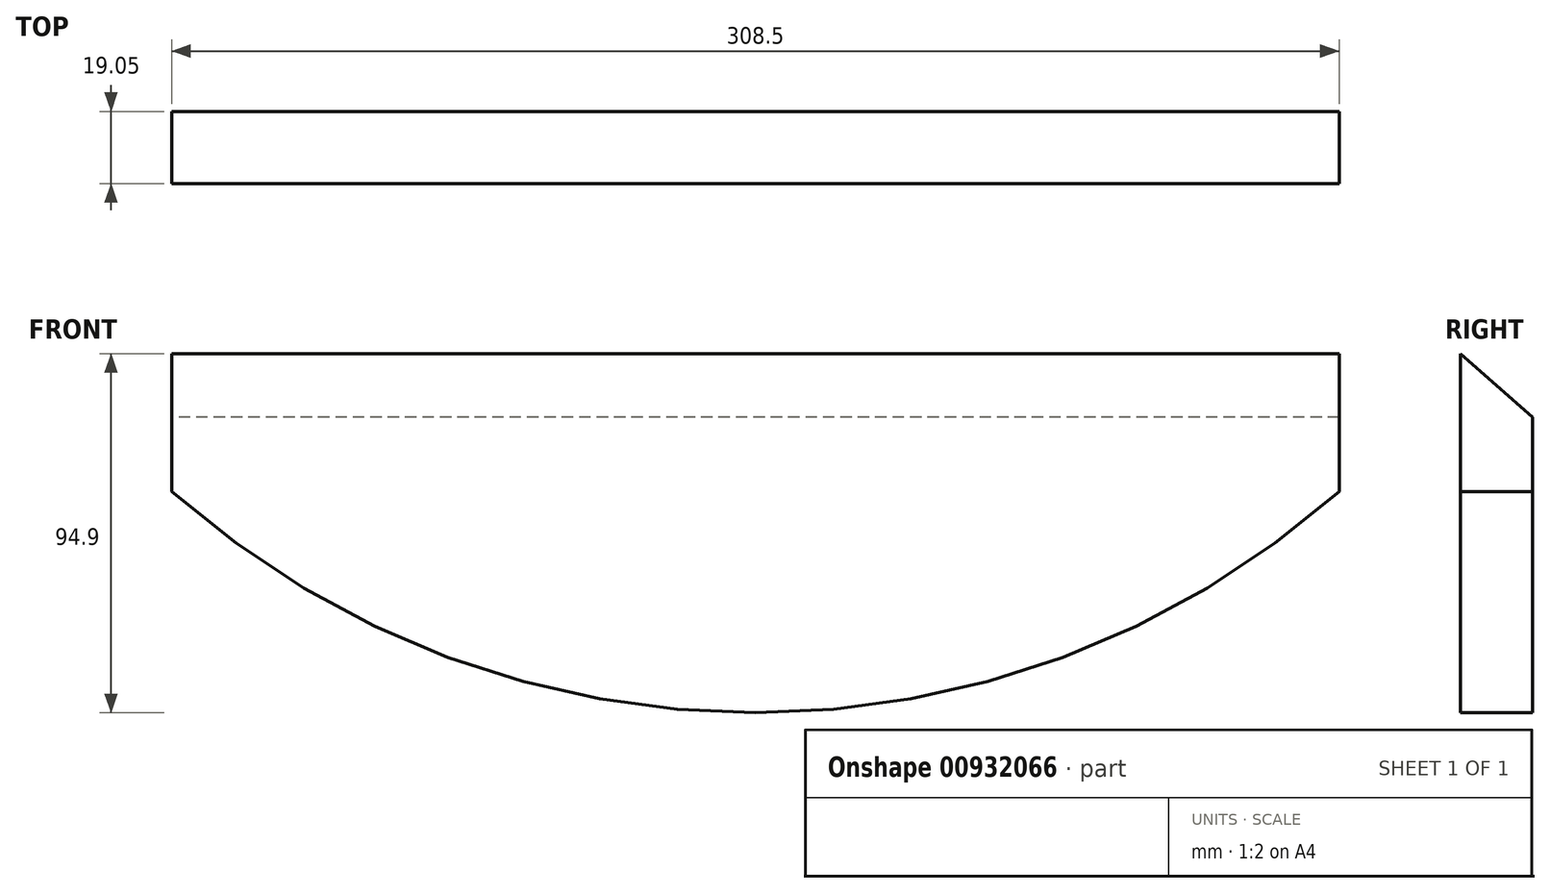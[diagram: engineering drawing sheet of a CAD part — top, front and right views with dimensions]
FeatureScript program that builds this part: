
annotation { "Feature Type Name" : "Feature", "Feature Type Description" : "" }
export const myFeature = defineFeature(function(context is Context, id is Id, definition is map)
    precondition{}
    {
        {
            var Q0;
            Q0=qCreatedBy(makeId("Front.planeOp"),FACE);
            var sketch = newSketch(context, id + "F0", { "sketchPlane" : qUnion([Q0])});
            skLineSegment(sketch, "E0", {"start": v(-154.25, 0) * mm, "end": v(154.25, 0) * mm});
            skArc(sketch, "E1", {"start": v(-154.25, -36.38) * mm, "mid": v(0, -94.9) * mm, "end": v(154.25, -36.38) * mm});
            skPoint(sketch, "E2", {"position": v(0, -94.9) * mm});
            skLineSegment(sketch, "E3", {"start": v(0, 137.66) * mm, "end": v(-110.88, -66.77) * mm, "construction": true});
            skLineSegment(sketch, "E4", {"start": v(-154.25, 0) * mm, "end": v(-154.25, -36.38) * mm});
            skLineSegment(sketch, "E5", {"start": v(154.25, 0) * mm, "end": v(154.25, -36.38) * mm});
            skLineSegment(sketch, "E6", {"start": v(-154.25, -18.2) * mm, "end": v(0, -18.2) * mm, "construction": true});
            skPoint(sketch, "E6.endSnap0", {"position": v(154.25, -18.2) * mm});
            skLineSegment(sketch, "E7", {"start": v(0, -18.2) * mm, "end": v(154.25, -18.2) * mm, "construction": true});
            skPoint(sketch, "E8.orphan", {"position": v(-187.44, 0) * mm});
            skSolve(sketch);
        }
        {
            var Q0;
            Q0 = qSketchRegion(id + "F0", true);
            extrude(context, id + "F1", {"entities" : qUnion([Q0]), "depth" : 19.05 * mm, "offsetDistance" : 25.4 * mm});
        }
        {
            var Q0;
            Q0=makeQuery(id+"F1.opExtrude","SWEPT_FACE",FACE,{"disambiguationData":[OSD([sQuery(id+"F0.wireOp",EDGE,"E4")])]});
            var sketch = newSketch(context, id + "F2", { "sketchPlane" : qUnion([Q0])});
            skLineSegment(sketch, "E9", {"start": v(0, 0) * mm, "end": v(0, -16.8) * mm});
            skLineSegment(sketch, "E10", {"start": v(0, -16.8) * mm, "end": v(19.05, 0) * mm});
            skLineSegment(sketch, "E11", {"start": v(19.05, 0) * mm, "end": v(0, 0) * mm});
            skSolve(sketch);
        }
        {
            var Q0;
            Q0 = qSketchRegion(id + "F2", true);
            var Q1;
            Q1=makeQuery(id+"F1.opExtrude","SWEPT_FACE",FACE,{"disambiguationData":[OSD([sQuery(id+"F0.wireOp",EDGE,"E5")])]});
            extrude(context, id + "F3", {"entities" : qUnion([Q0]), "operationType" : NewBodyOperationType.REMOVE, "endBound" : BoundingType.UP_TO_SURFACE, "oppositeDirection" : true, "depth" : 25.4 * mm, "endBoundEntityFace" : qUnion([Q1]), "offsetDistance" : 25.4 * mm});
        }
    });
